# Revit family: Deca_Cuba de sobrepor com saboneteira grelha_Cubas Espec._L.1044C
name_source: partatom
category: Plumbing Fixtures
units: mm (PartAtom-declared; Revit-internal decimal feet)

## family parameters
Cut with Voids When Loaded = No
Host = Face
Part Type = Normal
Room Calculation Point = No
Round Connector Dimension = Use Radius
Shared = No

## types (2) — shared parameters
Acompanha o Produto = SOMENTE GRELHA
Aprovado por = quattroD
Atendimento ao Cliente = 0800-0117073
Categoria = CUBAS
Composição Anel Vedação = -
Composição Assento = -
Composição Básica = Argila, feldspato, caulim, vidrados e corantes inorgânicos.
Composição Componente = Liga de cobre (bronze e latão), elastômeros e plásticos de engenharia.
Consumo = -
Cor Interna = -
Cor Principal = Ébano
Cor Secundária = -
Criado por = quattroD
Código Pai = L.1044C
Description = Cuba de sobrepor com saboneteira grelha
Diâmetro Ponto de Esgoto = 25 mm  [stored 0.082021 ft]
Informações Complementares = -
Itens de Instalação = 1680.BL.100.112.MT; 1680.C.100.112; 1682.C.100.112; 1684.BL.100.112.MT; 1684.C.100.112
Linha = Cubas Espec.
Manufacturer = Deca
Material = Deca_Ébano
Norma = NBR-16728-1;NBR-16728-2
Peso Líquido (Kg) = 22.917
Pressão máx. funcionamento = -
Pressão mín. Aquec. Acúmulo = -
Pressão mín. Aquec. Passagem = -
Pressão mín. funcionamento = -
Raio Ponto de Esgoto = 13 mm
Saída de Esgoto = Válvula Curta
Segmento = Banheiro Luxo
Tipo de dispositivo economizador = -
Tipo de mecanismo utilizado = -
Tipo de rosca de entrada = -
Tipo de rosca de saída = -
URL = www.deca.com.br
Vazão na Pressão máx. (L/min) = -
Vazão na Pressão mín. (L/min) = -
zero-valued in all types: Default Elevation, WFU

## per-type parameters (varying)
| type | Cores Componente | Material Secundário | Model |
| L.1044.BL.MT.95_Ébano | Black Matte | Deca_Black Matte | L.1044.BL.MT.95 |
| L.1044C.95_Ébano | Cromado | Deca_Cromado | L.1044C.95 |

note: [stored X ft] marks values corroborated as IEEE doubles in the binary element streams (Revit-internal decimal feet)

## geometry (parser evidence)
native form markers: Sweep x2
no freeform markers — native parametric forms only
